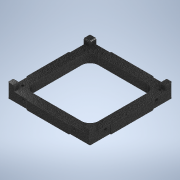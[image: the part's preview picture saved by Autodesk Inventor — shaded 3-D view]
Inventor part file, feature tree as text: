
AUTODESK INVENTOR PART (.ipt)
format: ipt  version: 2022 (Build 260153000, 153)  size: 351,232 bytes
history: native  units: mm
features: extrude x9, sketch x9, projected_geometry x4, fillet x2, chamfer x1
ambient origin geometry x8: Origin, YZ Plane, XZ Plane, XY Plane, X Axis, Y Axis, Z Axis, Center Point
bodies: Solid1 (feature_tree)
feature tree (25):
  extrude  "Extrusion1"  Depth=73.66mm
  extrude  "Extrusion2"  Depth=2.54mm
  extrude  "Extrusion3"  Depth=100.0mm
  fillet  "Fillet1"  Radius=100.0mm
  extrude  "Extrusion4"  Depth=10.0mm TaperAngle=0.0deg
  chamfer  "Chamfer1"  Distance=6.2mm
  extrude  "Extrusion5"  Depth=1.2mm
  fillet  "Fillet2"  Radius=25.0mm
  extrude  "Extrusion6"  Depth=25.0mm
  extrude  "Extrusion7"  TaperAngle=0.0deg  [1 undecoded]
  extrude  "Extrusion8"  Depth=6.5mm TaperAngle=360.0deg
  extrude  "Extrusion9"  Depth=1.0mm
  sketch  "Sketch1"  dims[d0=73.66mm d1=80.01mm]
  sketch  "Sketch4"  dims[d2=85.730001mm d3=2.54mm]
  projected_geometry  "Projected Loop2"
  sketch  "Sketch5"  dims[d4=3.81mm d6=2.9mm d7=100.0mm]
  projected_geometry  "Projected Loop3"
  sketch  "Sketch6"  dims[d8=100.0mm d10=10.0mm d11=0.0mm]
  projected_geometry  "Projected Loop4"
  sketch  "Sketch7"  dims[d13=4.5mm]
  projected_geometry  "Projected Loop5"
  sketch  "Sketch8"  dims[d14=4.5mm]
  sketch  "Sketch9"  dims[d15=4.5mm]
  sketch  "Sketch10"  dims[d16=4.5mm d17=6.2mm d18=0.0mm]
  sketch  "Sketch11"  dims[d19=1.2mm d20=1.2mm d21=25.0mm d22=25.0mm d23=0.0mm d24=0.0mm d25=40.0mm d27=360.0deg d29=1.0mm d30=7.3mm d31=7.3mm d32=6.5mm d33=0.0mm d34=1.0mm d35=2.0mm d36=45.0deg d37=40.0mm d39=360.0deg d50=11.0mm d51=11.0mm d52=11.0mm d53=11.0mm d54=10.0mm d55=0.0mm d56=10.0mm d57=30.5mm d58=30.5mm d59=4.2mm d60=4.2mm d61=7.7mm d62=0.0mm d63=4.2mm d64=4.2mm d67=6.5mm d68=0.0mm d69=4.2mm d70=7.7mm d71=0.0mm d72=6.5mm d73=0.0mm d75=3.2mm d76=3.2mm d77=3.2mm d78=19.5mm d79=19.5mm]
note: 1 required parameter value undecoded (feature->parameter linkage not recoverable at this tier; creation-order binding heuristic only, values carry confidence <= 0.55)
